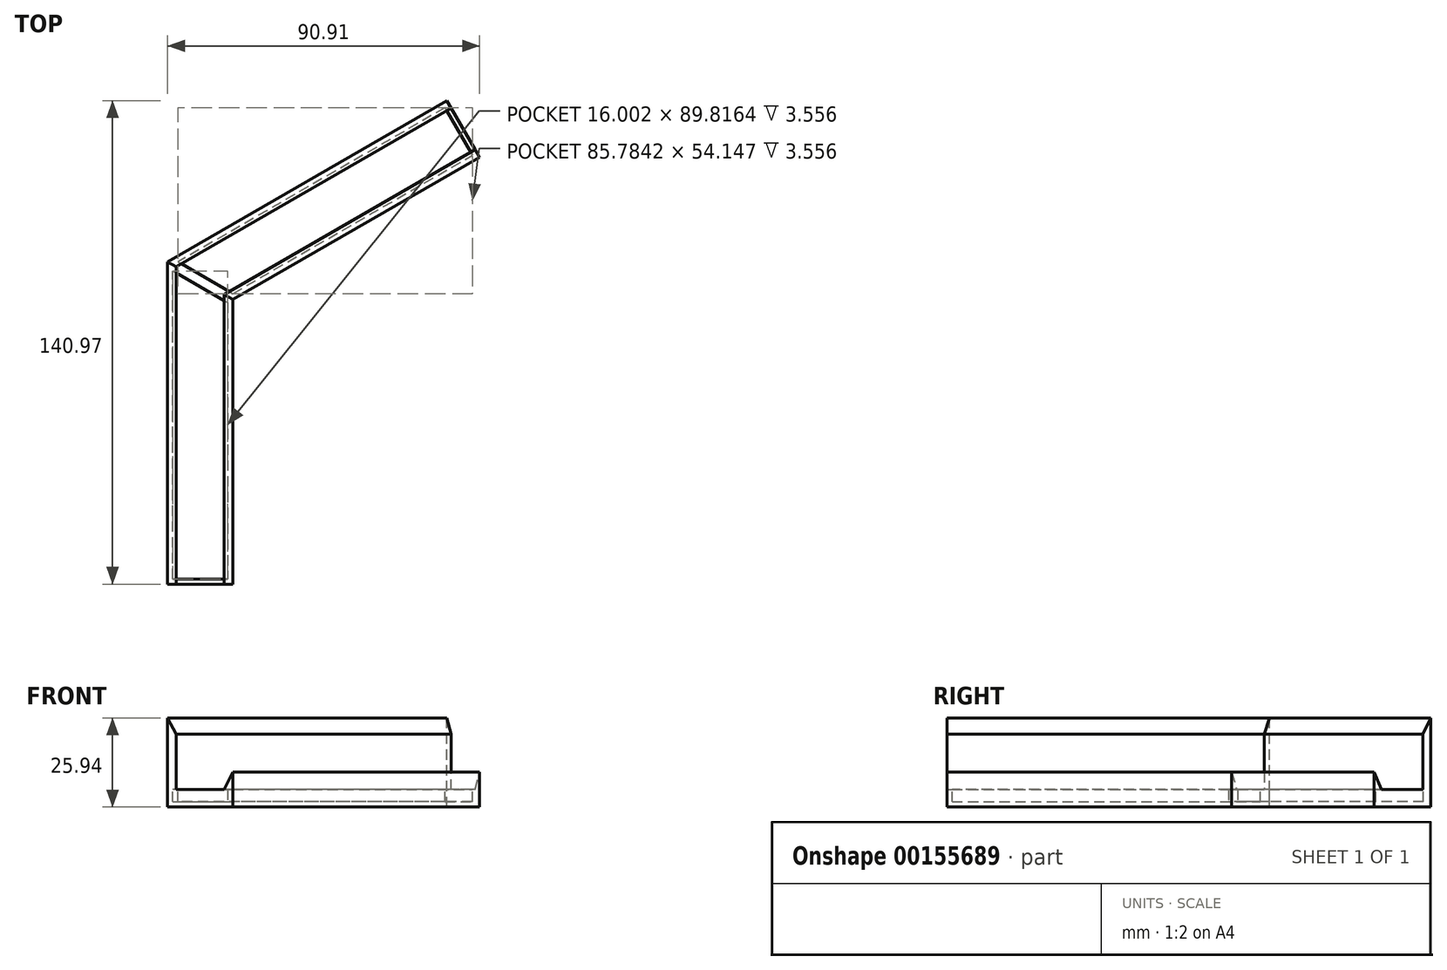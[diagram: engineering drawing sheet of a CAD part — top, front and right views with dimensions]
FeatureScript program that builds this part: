
annotation { "Feature Type Name" : "Feature", "Feature Type Description" : "" }
export const myFeature = defineFeature(function(context is Context, id is Id, definition is map)
    precondition{}
    {
        {
            var Q0;
            Q0=qCreatedBy(makeId("Front.planeOp"),FACE);
            var sketch = newSketch(context, id + "F0", { "sketchPlane" : qUnion([Q0])});
            skLineSegment(sketch, "E0", {"start": v(-5.26, 0) * mm, "end": v(13.79, 0) * mm});
            skLineSegment(sketch, "E1", {"start": v(-5.26, 0) * mm, "end": v(-5.26, 25.94) * mm});
            skLineSegment(sketch, "E2", {"start": v(-5.26, 25.94) * mm, "end": v(-2.72, 21.23) * mm});
            skLineSegment(sketch, "E3", {"start": v(13.79, 0) * mm, "end": v(13.79, 10.16) * mm});
            skLineSegment(sketch, "E4", {"start": v(11.25, 5.08) * mm, "end": v(13.79, 10.16) * mm});
            skLineSegment(sketch, "E5", {"start": v(11.25, 5.08) * mm, "end": v(-2.72, 5.08) * mm});
            skLineSegment(sketch, "E6", {"start": v(-2.72, 5.08) * mm, "end": v(-2.72, 21.23) * mm});
            skPoint(sketch, "E7.orphan", {"position": v(8.7, 0) * mm});
            skPoint(sketch, "E8.end.orphan", {"position": v(11.25, 0) * mm});
            skSolve(sketch);
        }
        {
            var Q0;
            Q0 = qSketchRegion(id + "F0", true);
            extrude(context, id + "F1", {"entities" : qUnion([Q0]), "depth" : 93.98 * mm});
        }
        {
            var Q0;
            Q0=makeQuery(id+"F1.opExtrude","SWEPT_FACE",FACE,{"disambiguationData":[OSD([sQuery(id+"F0.wireOp",EDGE,"E0")])]});
            var sketch = newSketch(context, id + "F2", { "sketchPlane" : qUnion([Q0])});
            skLineSegment(sketch, "E9", {"start": v(-5.26, 0) * mm, "end": v(13.79, 11) * mm});
            skLineSegment(sketch, "E10", {"start": v(13.79, 11) * mm, "end": v(13.79, 0) * mm});
            skLineSegment(sketch, "E11", {"start": v(-5.26, 0) * mm, "end": v(13.79, 0) * mm});
            skSolve(sketch);
        }
        {
            var Q0;
            Q0 = qSketchRegion(id + "F2", true);
            extrude(context, id + "F3", {"entities" : qUnion([Q0]), "operationType" : NewBodyOperationType.REMOVE, "oppositeDirection" : true, "depth" : 50.8 * mm});
        }
        {
            var Q0;
            {var subQ0=makeQuery(id+"F1.opExtrude","SWEPT_FACE",FACE,{"disambiguationData":[OSD([sQuery(id+"F0.wireOp",EDGE,"E5")])]});Q0=makeQuery(id+"F5.boolean.opBoolean","MERGE",FACE,{"derivedFrom":[subQ0,makeQuery(id+"F5.opPattern","COPY",FACE,{"derivedFrom":subQ0,"instanceName":"1"})]});}
            shell(context, id + "F4", {"entities" : qUnion([Q0]), "thickness" : 1.52 * mm});
        }
        {
            var Q0;
            Q0=makeQuery(id+"F1.opExtrude","SWEPT_BODY",BODY,{"disambiguationData":[OSD([sQuery(id+"F0.wireOp",EDGE,"E0"),sQuery(id+"F0.wireOp",EDGE,"E1"),sQuery(id+"F0.wireOp",EDGE,"E2"),sQuery(id+"F0.wireOp",EDGE,"E3"),sQuery(id+"F0.wireOp",EDGE,"E4"),sQuery(id+"F0.wireOp",EDGE,"E5"),sQuery(id+"F0.wireOp",EDGE,"E6")])]});
            var Q1;
            Q1=makeQuery(id+"F3.boolean.opBoolean","COPY",FACE,{"derivedFrom":makeQuery(id+"F3.opExtrude","SWEPT_FACE",FACE,{"disambiguationData":[OSD([sQuery(id+"F2.wireOp",EDGE,"E9")])]})});
            mirror(context, id + "F5", {"operationType" : NewBodyOperationType.ADD, "entities" : qUnion([Q0]), "mirrorPlane" : qUnion([Q1])});
        }
    });
